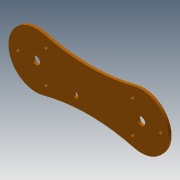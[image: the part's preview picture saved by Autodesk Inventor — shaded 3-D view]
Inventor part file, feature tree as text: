
AUTODESK INVENTOR PART (.ipt)
format: ipt  version: 2013 (Build 170138000, 138)  size: 198,144 bytes
history: native  units: mm
features: extrude x11, sketch x11
ambient origin geometry x8: Origin, YZ Plane, XZ Plane, XY Plane, X Axis, Y Axis, Z Axis, Center Point
bodies: Solid1 (feature_tree)
feature tree (22):
  extrude  "Extrusion1"  Depth=2.0mm TaperAngle=0.0deg
  extrude  "Extrusion2"  Depth=3.0mm
  extrude  "Extrusion3"  Depth=2.0mm TaperAngle=0.0deg
  extrude  "Extrusion4"  Depth=6.0mm
  extrude  "Extrusion5"  Depth=3.0mm
  extrude  "Extrusion6"  Depth=3.0mm
  extrude  "Extrusion7"  Depth=10.0mm TaperAngle=0.0deg
  extrude  "Extrusion8"  Depth=2.0mm TaperAngle=0.0deg
  extrude  "Extrusion9"  Depth=6.0mm
  extrude  "Extrusion10"  TaperAngle=120.0deg  [1 undecoded]
  extrude  "Extrusion11"  Depth=3.0mm
  sketch  "Sketch1"  dims[d1=6.0mm d3=10.0mm d5=4.0mm d7=4.0mm d8=2.0mm d9=0.0mm]
  sketch  "Sketch2"  dims[d11=3.0mm d14=3.0mm]
  sketch  "Sketch3"  dims[d15=3.0mm d16=2.0mm d17=0.0mm]
  sketch  "Sketch4"  dims[d18=10.5mm d19=6.0mm]
  sketch  "Sketch5"  dims[d20=2.0mm d21=0.0mm d33=3.0mm]
  sketch  "Sketch6"  dims[d34=3.0mm d35=3.0mm]
  sketch  "Sketch7"  dims[d36=2.0mm d37=0.0mm d38=10.0mm d39=0.0mm]
  sketch  "Sketch8"  dims[d40=2.0mm d41=0.0mm d42=2.0mm d43=0.0mm]
  sketch  "Sketch9"  dims[d44=2.0mm d45=0.0mm d47=6.0mm]
  sketch  "Sketch10"  dims[d48=3.0mm d49=120.0deg]
  sketch  "Sketch11"  dims[d50=120.0deg d51=3.0mm d52=3.0mm d53=2.0mm d54=0.0mm d55=30.0mm d56=8.0mm d57=4.0mm d58=2.0mm d59=0.0mm d63=4.0mm d64=2.0mm d65=0.0mm]
note: 1 required parameter value undecoded (feature->parameter linkage not recoverable at this tier; creation-order binding heuristic only, values carry confidence <= 0.55)
